# Revit family: Faucet-Lavatory-KOHLER-STANCE-K-72843T_1
name_source: partatom
category: Plumbing Fixtures
revit_build: Autodesk Revit 2017 (Build: 20160225_1515(x64)
units: mm (PartAtom-declared; Revit-internal decimal feet)

## family parameters
Cut with Voids When Loaded = No
Host = Face
OmniClass Number = 23.31.11.00
OmniClass Title = Faucets
Part Type = Normal
Room Calculation Point = No
Round Connector Dimension = Use Diameter
Shared = No

## types (4) — shared parameters
ADA Compliant = No
Assembly Code = D2010
CW Connection = Yes
Cold Water Inlet = Cold Water Inlet
Date Modified = 08/21/2020
Default Elevation = 36"
Flow Rate = 0 GPM
HW Connection = Yes
Handle Clearance = 3 9/16"
Height = 12 3/16"
Hot Water Inlet = Hot Water Inlet
Length = 6 7/16"
Manufacturer = KOHLER Co.
Master Format 2014 = 22 41 39
Master Format 2014 Name = Residential Faucets, Supplies, and Trim
Material = Premium Metal Construction
Pressure = 0.00 psi
Product Name = STANCE
Spout Reach = 6 7/16"
URL = http://www.kohler.com.cn
Vent Connection = No
Waste Connection = No
Waste Water Outlet = Waste Water Outlet
WaterSense Certified = No
Width = 2 1/8"

## per-type parameters (varying)
| type | Description | Drain Included | Finish | Model | Product Documentation Link | Product Page URL | Type |
| CP- Polished Chrome | Single Handle Bowl Faucet (Precise Style) | Yes | Kohler-Metal-CP-Polished_Chrome | K-72843T-4-CP | https://files.kohler.com.cn | https://www.kohler.com.cn | 1 |
| Without Drain, CP- Polished Chrome | Single Handle Bowl Faucet (Precise Style) Without Drain | No | Kohler-Metal-CP-Polished_Chrome | K-72843T-4ND-CP |  |  | 3 |
| 2BL- Original Black | Single Handle Bowl Faucet (Precise Style) | Yes | Kohler-Metal-2BL-Original_Black | K-72843T-4-2BL | https://files.kohler.com.cn | https://www.kohler.com.cn | 2 |
| Without Drain, 2BL- Original Black | Single Handle Bowl Faucet (Precise Style) Without Drain | No | Kohler-Metal-2BL-Original_Black | K-72843T-4ND-2BL |  |  | 4 |

## geometry (parser evidence)
native form markers: Sweep x5
no freeform markers — native parametric forms only
